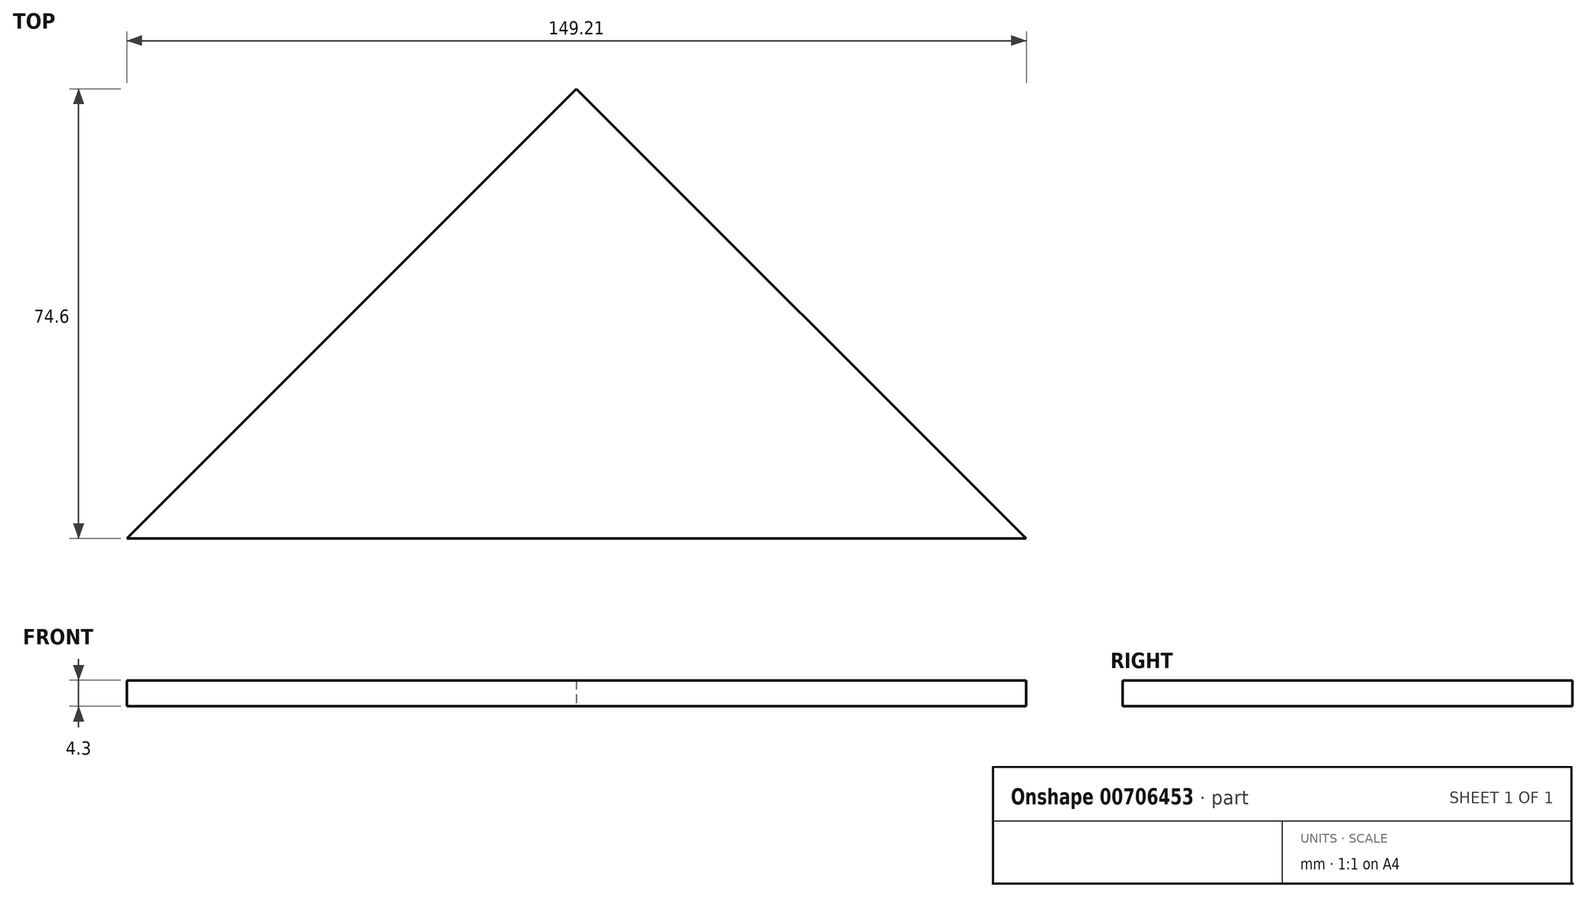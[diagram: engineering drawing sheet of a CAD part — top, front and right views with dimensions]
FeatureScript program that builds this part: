
annotation { "Feature Type Name" : "Feature", "Feature Type Description" : "" }
export const myFeature = defineFeature(function(context is Context, id is Id, definition is map)
    precondition{}
    {
        {
            var Q0;
            Q0=qCreatedBy(makeId("Top.planeOp"),FACE);
            var sketch = newSketch(context, id + "F0", { "sketchPlane" : qUnion([Q0])});
            skLineSegment(sketch, "E0", {"start": v(-74.6, 0) * mm, "end": v(0, 74.6) * mm});
            skLineSegment(sketch, "E1", {"start": v(0, 74.6) * mm, "end": v(74.62, 0) * mm});
            skLineSegment(sketch, "E2", {"start": v(74.62, 0) * mm, "end": v(0, 0) * mm});
            skLineSegment(sketch, "E3", {"start": v(0, 0) * mm, "end": v(-74.6, 0) * mm});
            skSolve(sketch);
        }
        {
            var Q0;
            Q0=makeQuery(id+"F0.imprint","IMPRINT",FACE,{"disambiguationData":[TD([[makeQuery(id+"F0.imprint","IMPRINT",EDGE,{"derivedFrom":sQuery(id+"F0.wireOp",EDGE,"E0")}),-1.0]])]});
            extrude(context, id + "F1", {"entities" : qUnion([Q0]), "depth" : 4.3 * mm, "offsetDistance" : 25 * mm});
        }
    });
